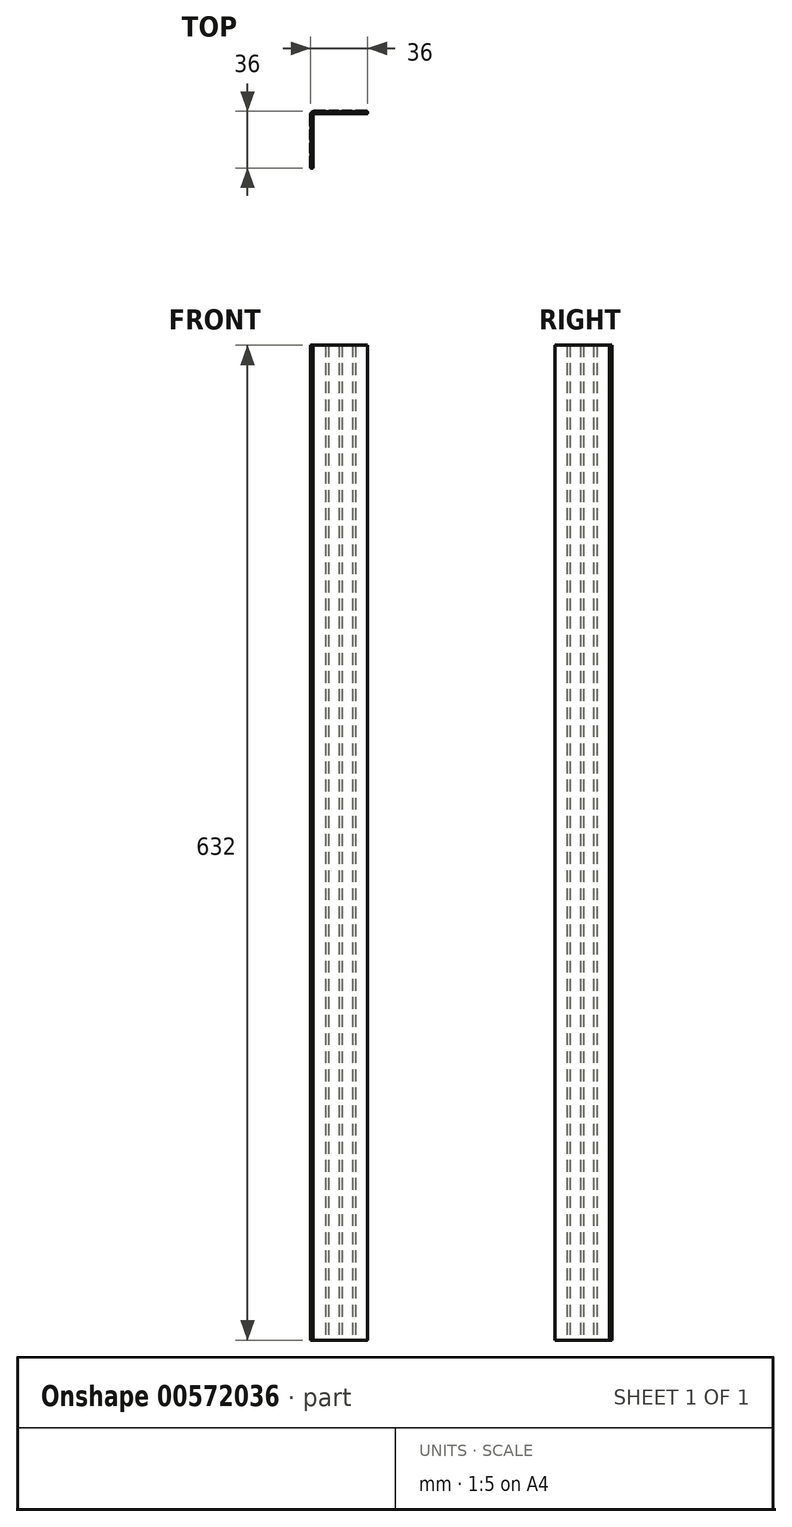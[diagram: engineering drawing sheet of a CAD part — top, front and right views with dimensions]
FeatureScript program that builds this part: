
annotation { "Feature Type Name" : "Feature", "Feature Type Description" : "" }
export const myFeature = defineFeature(function(context is Context, id is Id, definition is map)
    precondition{}
    {
        {
            var Q0;
            Q0=qCreatedBy(makeId("Top.planeOp"),FACE);
            var sketch = newSketch(context, id + "F0", { "sketchPlane" : qUnion([Q0])});
            skLineSegment(sketch, "E0", {"start": v(0, 0) * mm, "end": v(0, 7.5) * mm});
            skPoint(sketch, "E1.visualSharp", {"position": v(0, 36) * mm});
            skArc(sketch, "E1.filletArc", {"start": v(0.59, 35.41) * mm, "mid": v(0.15, 34.77) * mm, "end": v(0, 34) * mm});
            skLineSegment(sketch, "E2.1", {"start": v(1.5, 0) * mm, "end": v(1.5, 33.5) * mm});
            skLineSegment(sketch, "E3", {"start": v(1.5, 0) * mm, "end": v(0, 0) * mm});
            skPoint(sketch, "E4.visualSharp", {"position": v(1.5, 34.5) * mm});
            skArc(sketch, "E4.filletArc", {"start": v(1.8, 34.2) * mm, "mid": v(1.58, 33.88) * mm, "end": v(1.5, 33.5) * mm});
            skLineSegment(sketch, "E5.bottom", {"start": v(0, 18) * mm, "end": v(0.25, 18) * mm});
            skLineSegment(sketch, "E5.top", {"start": v(0, 16) * mm, "end": v(0.25, 16) * mm});
            skLineSegment(sketch, "E5.right", {"start": v(0.25, 18) * mm, "end": v(0.25, 16) * mm});
            skPoint(sketch, "E5.middle", {"position": v(0, 17) * mm});
            skLineSegment(sketch, "E6", {"start": v(0, 0) * mm, "end": v(-1.84, 0) * mm, "construction": true});
            skLineSegment(sketch, "E7", {"start": v(-1.84, 0) * mm, "end": v(-1.84, 17) * mm, "construction": true});
            skPoint(sketch, "E7.endSnap0", {"position": v(-0.25, 17) * mm});
            skLineSegment(sketch, "E8", {"start": v(-1.84, 8.5) * mm, "end": v(0, 8.5) * mm, "construction": true});
            skLineSegment(sketch, "E9.bottom", {"start": v(0.25, 9.5) * mm, "end": v(0, 9.5) * mm});
            skLineSegment(sketch, "E9.top", {"start": v(0.25, 7.5) * mm, "end": v(0, 7.5) * mm});
            skLineSegment(sketch, "E9.left", {"start": v(0.25, 9.5) * mm, "end": v(0.25, 7.5) * mm});
            skPoint(sketch, "E9.middle", {"position": v(0, 8.5) * mm});
            skLineSegment(sketch, "E10", {"start": v(-1.84, 17) * mm, "end": v(-1.84, 34) * mm, "construction": true});
            skLineSegment(sketch, "E11", {"start": v(-1.84, 25.5) * mm, "end": v(0, 25.5) * mm, "construction": true});
            skLineSegment(sketch, "E12.bottom", {"start": v(0.25, 26.5) * mm, "end": v(0, 26.5) * mm});
            skLineSegment(sketch, "E12.top", {"start": v(0.25, 24.5) * mm, "end": v(0, 24.5) * mm});
            skLineSegment(sketch, "E12.left", {"start": v(0.25, 26.5) * mm, "end": v(0.25, 24.5) * mm});
            skPoint(sketch, "E12.middle", {"position": v(0, 25.5) * mm});
            skPoint(sketch, "E13.end.orphan", {"position": v(36, 36) * mm});
            skLineSegment(sketch, "E14.trimOffspring", {"start": v(0, 9.5) * mm, "end": v(0, 16) * mm});
            skPoint(sketch, "E15.orphan", {"position": v(-0.25, 9.5) * mm});
            skPoint(sketch, "E16.orphan", {"position": v(-0.25, 7.5) * mm});
            skPoint(sketch, "E17.orphan", {"position": v(-0.25, 16) * mm});
            skLineSegment(sketch, "E18.trimOffspring", {"start": v(0, 18) * mm, "end": v(0, 24.5) * mm});
            skPoint(sketch, "E19.orphan", {"position": v(-0.25, 18) * mm});
            skLineSegment(sketch, "E20.trimOffspring", {"start": v(0, 26.5) * mm, "end": v(0, 34) * mm});
            skPoint(sketch, "E21.orphan", {"position": v(-0.25, 24.5) * mm});
            skPoint(sketch, "E22.orphan", {"position": v(-0.25, 26.5) * mm});
            skLineSegment(sketch, "E23.MirrorCS", {"start": v(11.5, 35.75) * mm, "end": v(11.5, 36) * mm});
            skLineSegment(sketch, "E24.MirrorCS", {"start": v(26.5, 35.75) * mm, "end": v(28.5, 35.75) * mm});
            skLineSegment(sketch, "E25.MirrorCS", {"start": v(28.5, 35.75) * mm, "end": v(28.5, 36) * mm});
            skLineSegment(sketch, "E26.MirrorCS", {"start": v(9.5, 35.75) * mm, "end": v(11.5, 35.75) * mm});
            skLineSegment(sketch, "E27.MirrorCS", {"start": v(9.5, 35.75) * mm, "end": v(9.5, 36) * mm});
            skLineSegment(sketch, "E28.MirrorCS", {"start": v(20, 36) * mm, "end": v(20, 35.75) * mm});
            skLineSegment(sketch, "E29.MirrorCS", {"start": v(26.5, 35.75) * mm, "end": v(26.5, 36) * mm});
            skLineSegment(sketch, "E30.MirrorCS", {"start": v(18, 35.75) * mm, "end": v(20, 35.75) * mm});
            skLineSegment(sketch, "E31.MirrorCS", {"start": v(18, 36) * mm, "end": v(18, 35.75) * mm});
            skArc(sketch, "E32.MirrorCS", {"start": v(1.8, 34.2) * mm, "mid": v(2.12, 34.42) * mm, "end": v(2.5, 34.5) * mm});
            skLineSegment(sketch, "E33.MirrorCS", {"start": v(36, 34.5) * mm, "end": v(36, 36) * mm});
            skArc(sketch, "E34.MirrorCS", {"start": v(0.59, 35.41) * mm, "mid": v(1.23, 35.85) * mm, "end": v(2, 36) * mm});
            skLineSegment(sketch, "E35.MirrorCS", {"start": v(10.5, 37.84) * mm, "end": v(10.5, 36) * mm, "construction": true});
            skLineSegment(sketch, "E36.MirrorCS", {"start": v(36, 36) * mm, "end": v(36, 37.84) * mm, "construction": true});
            skPoint(sketch, "E37.MirrorP", {"position": v(19, 36.25) * mm});
            skLineSegment(sketch, "E38.MirrorCS", {"start": v(27.5, 37.84) * mm, "end": v(27.5, 36) * mm, "construction": true});
            skPoint(sketch, "E39.MirrorP", {"position": v(19, 36) * mm});
            skLineSegment(sketch, "E40.MirrorCS", {"start": v(36, 34.5) * mm, "end": v(2.5, 34.5) * mm});
            skPoint(sketch, "E41.MirrorP", {"position": v(27.5, 36) * mm});
            skLineSegment(sketch, "E42.MirrorCS", {"start": v(36, 36) * mm, "end": v(28.5, 36) * mm});
            skLineSegment(sketch, "E43.MirrorCS", {"start": v(19, 37.84) * mm, "end": v(2, 37.84) * mm, "construction": true});
            skPoint(sketch, "E44.MirrorP", {"position": v(28.5, 36.25) * mm});
            skLineSegment(sketch, "E45.MirrorCS", {"start": v(18, 36) * mm, "end": v(11.5, 36) * mm});
            skPoint(sketch, "E46.MirrorP", {"position": v(18, 36.25) * mm});
            skPoint(sketch, "E47.MirrorP", {"position": v(10.5, 36) * mm});
            skPoint(sketch, "E48.MirrorP", {"position": v(9.5, 36.25) * mm});
            skPoint(sketch, "E49.MirrorP", {"position": v(20, 36.25) * mm});
            skPoint(sketch, "E50.MirrorP", {"position": v(26.5, 36.25) * mm});
            skLineSegment(sketch, "E51.MirrorCS", {"start": v(9.5, 36) * mm, "end": v(2, 36) * mm});
            skLineSegment(sketch, "E52.MirrorCS", {"start": v(36, 37.84) * mm, "end": v(19, 37.84) * mm, "construction": true});
            skPoint(sketch, "E53.MirrorP", {"position": v(11.5, 36.25) * mm});
            skLineSegment(sketch, "E54.MirrorCS", {"start": v(26.5, 36) * mm, "end": v(20, 36) * mm});
            skSolve(sketch);
        }
        {
            var Q0;
            Q0=qSketchRegion(id+"F0",true);
            extrude(context, id + "F1", {"entities" : qUnion([Q0]), "depth" : 632 * mm, "offsetDistance" : 25 * mm});
        }
        {
            var Q0;
            Q0=makeQuery(id+"F1.opExtrude","SWEPT_EDGE",EDGE,{"disambiguationData":[OSD([sQuery(id+"F0.wireOp",EDGE,"E5.top"),sQuery(id+"F0.wireOp",EDGE,"E14.trimOffspring")])]});
            var Q1;
            Q1=makeQuery(id+"F1.opExtrude","SWEPT_EDGE",EDGE,{"disambiguationData":[OSD([sQuery(id+"F0.wireOp",EDGE,"E5.bottom"),sQuery(id+"F0.wireOp",EDGE,"E18.trimOffspring")])]});
            var Q2;
            Q2=makeQuery(id+"F1.opExtrude","SWEPT_EDGE",EDGE,{"disambiguationData":[OSD([sQuery(id+"F0.wireOp",EDGE,"E9.bottom"),sQuery(id+"F0.wireOp",EDGE,"E14.trimOffspring")])]});
            var Q3;
            Q3=makeQuery(id+"F1.opExtrude","SWEPT_EDGE",EDGE,{"disambiguationData":[OSD([sQuery(id+"F0.wireOp",EDGE,"E0"),sQuery(id+"F0.wireOp",EDGE,"E9.top")])]});
            var Q4;
            Q4=makeQuery(id+"F1.opExtrude","SWEPT_EDGE",EDGE,{"disambiguationData":[OSD([sQuery(id+"F0.wireOp",EDGE,"E12.bottom"),sQuery(id+"F0.wireOp",EDGE,"E20.trimOffspring")])]});
            var Q5;
            Q5=makeQuery(id+"F1.opExtrude","SWEPT_EDGE",EDGE,{"disambiguationData":[OSD([sQuery(id+"F0.wireOp",EDGE,"E12.top"),sQuery(id+"F0.wireOp",EDGE,"E18.trimOffspring")])]});
            var Q6;
            Q6=makeQuery(id+"F1.opExtrude","SWEPT_EDGE",EDGE,{"disambiguationData":[OSD([sQuery(id+"F0.wireOp",EDGE,"E27.MirrorCS"),sQuery(id+"F0.wireOp",EDGE,"E51.MirrorCS")])]});
            var Q7;
            Q7=makeQuery(id+"F1.opExtrude","SWEPT_EDGE",EDGE,{"disambiguationData":[OSD([sQuery(id+"F0.wireOp",EDGE,"E23.MirrorCS"),sQuery(id+"F0.wireOp",EDGE,"E45.MirrorCS")])]});
            var Q8;
            Q8=makeQuery(id+"F1.opExtrude","SWEPT_EDGE",EDGE,{"disambiguationData":[OSD([sQuery(id+"F0.wireOp",EDGE,"E31.MirrorCS"),sQuery(id+"F0.wireOp",EDGE,"E45.MirrorCS")])]});
            var Q9;
            Q9=makeQuery(id+"F1.opExtrude","SWEPT_EDGE",EDGE,{"disambiguationData":[OSD([sQuery(id+"F0.wireOp",EDGE,"E28.MirrorCS"),sQuery(id+"F0.wireOp",EDGE,"E54.MirrorCS")])]});
            var Q10;
            Q10=makeQuery(id+"F1.opExtrude","SWEPT_EDGE",EDGE,{"disambiguationData":[OSD([sQuery(id+"F0.wireOp",EDGE,"E29.MirrorCS"),sQuery(id+"F0.wireOp",EDGE,"E54.MirrorCS")])]});
            var Q11;
            Q11=makeQuery(id+"F1.opExtrude","SWEPT_EDGE",EDGE,{"disambiguationData":[OSD([sQuery(id+"F0.wireOp",EDGE,"E25.MirrorCS"),sQuery(id+"F0.wireOp",EDGE,"E42.MirrorCS")])]});
            var Q12;
            Q12=makeQuery(id+"F1.opExtrude","SWEPT_EDGE",EDGE,{"disambiguationData":[OSD([sQuery(id+"F0.wireOp",EDGE,"E33.MirrorCS"),sQuery(id+"F0.wireOp",EDGE,"E42.MirrorCS")])]});
            var Q13;
            Q13=makeQuery(id+"F1.opExtrude","SWEPT_EDGE",EDGE,{"disambiguationData":[OSD([sQuery(id+"F0.wireOp",EDGE,"E33.MirrorCS"),sQuery(id+"F0.wireOp",EDGE,"E40.MirrorCS")])]});
            var Q14;
            Q14=makeQuery(id+"F1.opExtrude","SWEPT_EDGE",EDGE,{"disambiguationData":[OSD([sQuery(id+"F0.wireOp",EDGE,"E0"),sQuery(id+"F0.wireOp",EDGE,"E3")])]});
            var Q15;
            Q15=makeQuery(id+"F1.opExtrude","SWEPT_EDGE",EDGE,{"disambiguationData":[OSD([sQuery(id+"F0.wireOp",EDGE,"E2.1"),sQuery(id+"F0.wireOp",EDGE,"E3")])]});
            fillet(context, id + "F2", {"entities" : qUnion([Q0, Q1, Q2, Q3, Q4, Q5, Q6, Q7, Q8, Q9, Q10, Q11, Q12, Q13, Q14, Q15]), "radius" : 0.2 * mm, "tangentPropagation" : true, "allowEdgeOverflow" : false});
        }
    });
